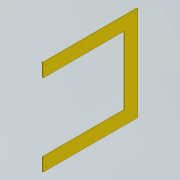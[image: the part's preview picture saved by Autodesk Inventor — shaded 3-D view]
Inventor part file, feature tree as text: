
AUTODESK INVENTOR PART (.ipt)
format: ipt  version: 2016 (Build 200138000, 138)  size: 105,984 bytes
history: native  units: mm
features: hole x4, extrude x1, sketch x1
ambient origin geometry x8: Origin, YZ Plane, XZ Plane, XY Plane, X Axis, Y Axis, Z Axis, Center Point
bodies: Solid1 (feature_tree)
feature tree (6):
  extrude  "Extrusion1"  Depth=360.0mm
  hole  "Hole1"  [1 undecoded]
  hole  "Hole2"  [1 undecoded]
  hole  "Hole3"  [1 undecoded]
  hole  "Hole4"  [1 undecoded]
  sketch  "Sketch1"  dims[d4=360.0mm d5=360.0mm d6=310.0mm d7=260.0mm d8=3.0mm d9=0.0mm d10=12.0mm d11=12.0mm d12=4.0mm d13=6.0mm d14=4.0mm d15=2.0mm d16=90.0deg d17=8.0mm d18=20.594885mm d19=12.0mm d20=12.0mm d21=4.0mm d22=6.0mm d23=4.0mm d24=2.0mm d25=90.0deg d26=8.0mm d27=20.594885mm d28=12.0mm d29=12.0mm d30=4.0mm d31=6.0mm d32=4.0mm d33=2.0mm d34=90.0deg d35=8.0mm d36=20.594885mm d37=12.0mm d38=12.0mm d39=4.0mm d40=6.0mm d41=4.0mm d42=2.0mm d43=90.0deg d44=8.0mm d45=20.594885mm]
note: 4 required parameter values undecoded (feature->parameter linkage not recoverable at this tier; creation-order binding heuristic only, values carry confidence <= 0.55)
